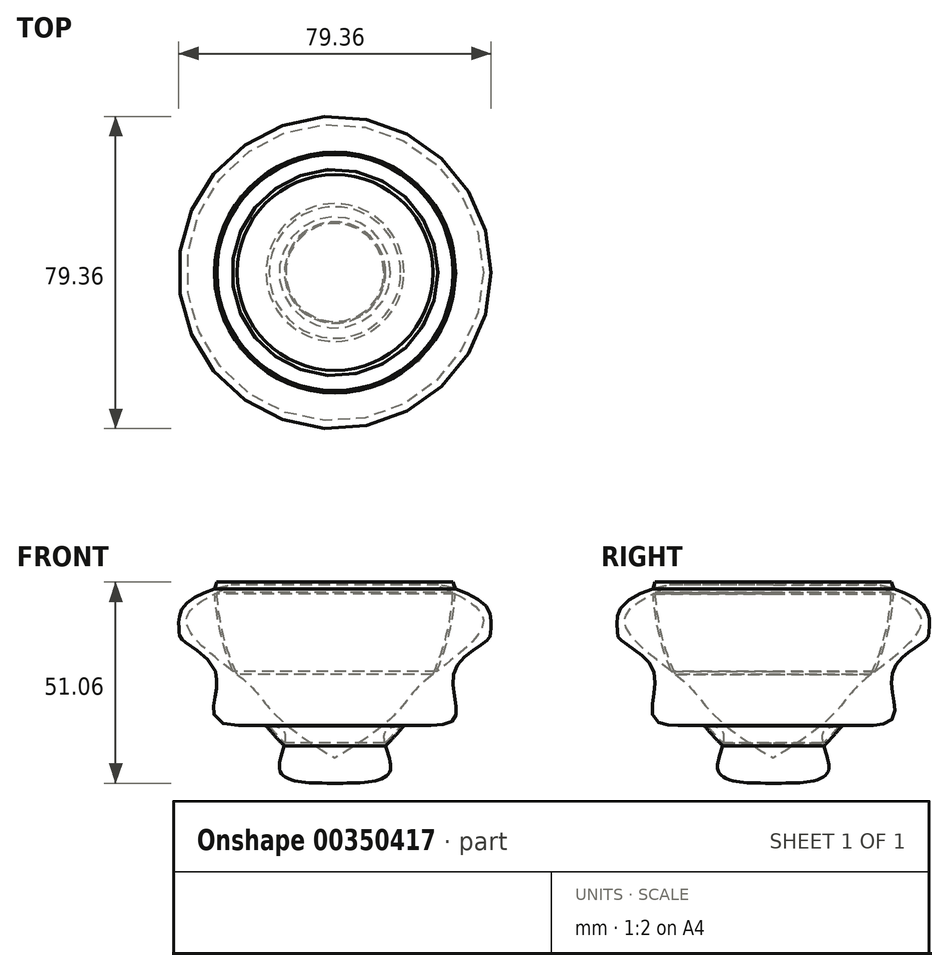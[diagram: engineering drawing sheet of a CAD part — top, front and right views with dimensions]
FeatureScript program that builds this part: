
annotation { "Feature Type Name" : "Feature", "Feature Type Description" : "" }
export const myFeature = defineFeature(function(context is Context, id is Id, definition is map)
    precondition{}
    {
        {
            var Q0;
            Q0=qCreatedBy(makeId("Front.planeOp"),FACE);
            var sketch = newSketch(context, id + "F0", { "sketchPlane" : qUnion([Q0])});
            skArc(sketch, "E0", {"start": v(-30.6, 49.28) * mm, "mid": v(-21.8, 20.6) * mm, "end": v(0, 0) * mm});
            skLineSegment(sketch, "E1", {"start": v(0, 0) * mm, "end": v(0, 49.8) * mm});
            skArc(sketch, "E2.0", {"start": v(-30.05, 51.05) * mm, "mid": v(-21.76, 21.71) * mm, "end": v(0.2, 0.57) * mm});
            skLineSegment(sketch, "E3", {"start": v(-30.6, 49.28) * mm, "end": v(-30.05, 51.05) * mm});
            skSolve(sketch);
        }
        {
            var Q0;
            {var subQ0=sQuery(id+"F0.wireOp",EDGE,"E0");Q0=makeQuery(id+"F0.imprint","IMPRINT",FACE,{"disambiguationData":[TD([[makeQuery(id+"F0.imprint","IMPRINT",EDGE,{"derivedFrom":subQ0}),1.0]])]});}
            var Q1;
            Q1=sQuery(id+"F0.wireOp",EDGE,"E1");
            revolve(context, id + "F1", {"entities" : qUnion([Q0]), "axis" : qUnion([Q1]), "revolveType" : RevolveType.FULL});
        }
        {
            var Q0;
            Q0=qCreatedBy(makeId("Front.planeOp"),FACE);
            var sketch = newSketch(context, id + "F2", { "sketchPlane" : qUnion([Q0])});
            skFitSpline(sketch, "E4", {"points": [v(0, 0) * mm, v(14.05, 3.29) * mm, v(13.02, 13.35) * mm, v(29.83, 15.81) * mm, v(30.3, 28.19) * mm, v(38.95, 36.58) * mm, v(39.6, 38.77) * mm, v(37.66, 45.74) * mm, v(26.18, 50.25) * mm, v(37.5, 42.43) * mm, v(22.43, 25.63) * mm, v(0, 6.37) * mm], "startDerivative": vector(192.27, -1.25) * mm, "endDerivative": vector(-407.1, -244) * mm});
            skLineSegment(sketch, "E5", {"start": v(0, 6.37) * mm, "end": v(0, 0) * mm});
            skSolve(sketch);
        }
        {
            var Q0;
            Q0=makeQuery(id+"F2.imprint","IMPRINT",FACE,{"disambiguationData":[TD([[makeQuery(id+"F2.imprint","IMPRINT",EDGE,{"derivedFrom":sQuery(id+"F2.wireOp",EDGE,"E4")}),1.0]])]});
            var Q1;
            Q1=sQuery(id+"F2.wireOp",EDGE,"E5");
            revolve(context, id + "F3", {"operationType" : NewBodyOperationType.ADD, "entities" : qUnion([Q0]), "axis" : qUnion([Q1]), "revolveType" : RevolveType.FULL});
        }
    });
